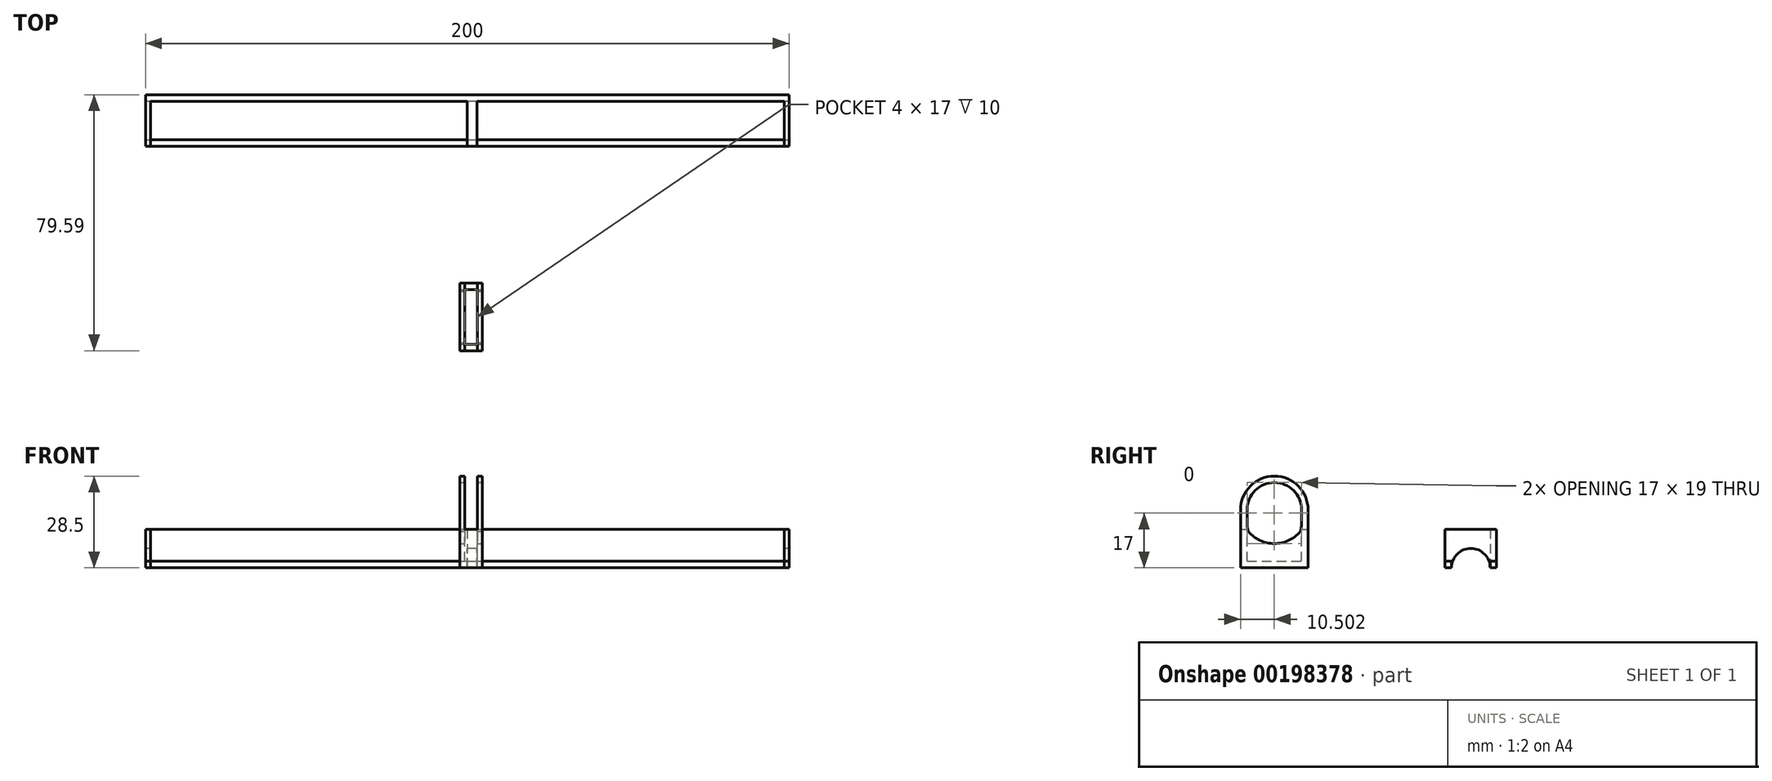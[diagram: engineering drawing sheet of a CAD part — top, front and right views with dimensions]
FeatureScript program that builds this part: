
annotation { "Feature Type Name" : "Feature", "Feature Type Description" : "" }
export const myFeature = defineFeature(function(context is Context, id is Id, definition is map)
    precondition{}
    {
        {
            assignVariable(context, id + "F0", {"name" : "railWidth", "anyValue" : 2});
        }
        {
            assignVariable(context, id + "F1", {"name" : "railSpace", "anyValue" : 12});
        }
        {
            var Q0;
            Q0=qCreatedBy(makeId("Top.planeOp"),FACE);
            var sketch = newSketch(context, id + "F2", { "sketchPlane" : qUnion([Q0])});
            skLineSegment(sketch, "E0", {"start": v(-153.07, 40.7) * mm, "end": v(46.93, 40.7) * mm});
            skLineSegment(sketch, "E1", {"start": v(-153.07, 38.7) * mm, "end": v(46.93, 38.7) * mm});
            skLineSegment(sketch, "E2", {"start": v(-153.07, 40.7) * mm, "end": v(-153.07, 38.7) * mm});
            skLineSegment(sketch, "E3", {"start": v(46.93, 40.7) * mm, "end": v(46.93, 38.7) * mm});
            skLineSegment(sketch, "E4", {"start": v(-153.07, 26.7) * mm, "end": v(46.93, 26.7) * mm});
            skLineSegment(sketch, "E5", {"start": v(-153.07, 24.7) * mm, "end": v(46.93, 24.7) * mm});
            skLineSegment(sketch, "E6", {"start": v(-153.07, 26.7) * mm, "end": v(-153.07, 24.7) * mm});
            skLineSegment(sketch, "E7", {"start": v(46.93, 26.7) * mm, "end": v(46.93, 24.7) * mm});
            skLineSegment(sketch, "E8", {"start": v(-153.07, 40.7) * mm, "end": v(-153.07, 24.7) * mm});
            skLineSegment(sketch, "E9", {"start": v(-151.57, 40.7) * mm, "end": v(-151.57, 24.7) * mm});
            skLineSegment(sketch, "E10", {"start": v(46.93, 40.7) * mm, "end": v(46.93, 24.7) * mm});
            skLineSegment(sketch, "E11", {"start": v(45.43, 40.7) * mm, "end": v(45.43, 24.7) * mm});
            skLineSegment(sketch, "E12", {"start": v(-53.07, 40.7) * mm, "end": v(-53.07, 24.7) * mm});
            skLineSegment(sketch, "E13", {"start": v(-50.07, 40.7) * mm, "end": v(-50.07, 24.7) * mm});
            skSolve(sketch);
        }
        {
            var Q0;
            {var subQ0=sQuery(id+"F2.wireOp",EDGE,"E9");var subQ1=sQuery(id+"F2.wireOp",EDGE,"E0");var subQ2=makeQuery(id+"F2.imprint","INTERSECT",VERTEX,{"derivedFrom":[subQ1,subQ0]});Q0=makeQuery(id+"F2.imprint","IMPRINT",FACE,{"disambiguationData":[TD([[makeQuery(id+"F2.imprint","IMPRINT",EDGE,{"disambiguationData":[TD([[subQ2,-1.0]])],"derivedFrom":subQ1}),-1.0]])]});}
            var Q1;
            {var subQ0=sQuery(id+"F2.wireOp",EDGE,"E12");var subQ1=sQuery(id+"F2.wireOp",EDGE,"E0");var subQ2=makeQuery(id+"F2.imprint","INTERSECT",VERTEX,{"derivedFrom":[subQ1,subQ0]});Q1=makeQuery(id+"F2.imprint","IMPRINT",FACE,{"disambiguationData":[TD([[makeQuery(id+"F2.imprint","IMPRINT",EDGE,{"disambiguationData":[TD([[subQ2,-1.0]])],"derivedFrom":subQ1}),-1.0]])]});}
            var Q2;
            {var subQ0=sQuery(id+"F2.wireOp",EDGE,"E11");var subQ1=sQuery(id+"F2.wireOp",EDGE,"E0");var subQ2=makeQuery(id+"F2.imprint","INTERSECT",VERTEX,{"derivedFrom":[subQ1,subQ0]});Q2=makeQuery(id+"F2.imprint","IMPRINT",FACE,{"disambiguationData":[TD([[makeQuery(id+"F2.imprint","IMPRINT",EDGE,{"disambiguationData":[TD([[subQ2,1.0]])],"derivedFrom":subQ1}),-1.0]])]});}
            var Q3;
            {var subQ0=sQuery(id+"F2.wireOp",EDGE,"E8");var subQ1=sQuery(id+"F2.wireOp",EDGE,"E0");var subQ2=makeQuery(id+"F2.imprint","INTERSECT",VERTEX,{"derivedFrom":[subQ1,subQ0]});Q3=makeQuery(id+"F2.imprint","IMPRINT",FACE,{"disambiguationData":[TD([[makeQuery(id+"F2.imprint","IMPRINT",EDGE,{"disambiguationData":[TD([[subQ2,-1.0]])],"derivedFrom":subQ1}),-1.0]])]});}
            var Q4;
            {var subQ0=sQuery(id+"F2.wireOp",EDGE,"E10");var subQ1=sQuery(id+"F2.wireOp",EDGE,"E0");var subQ2=makeQuery(id+"F2.imprint","INTERSECT",VERTEX,{"derivedFrom":[subQ1,subQ0]});Q4=makeQuery(id+"F2.imprint","IMPRINT",FACE,{"disambiguationData":[TD([[makeQuery(id+"F2.imprint","IMPRINT",EDGE,{"disambiguationData":[TD([[subQ2,1.0]])],"derivedFrom":subQ1}),-1.0]])]});}
            var Q5;
            {var subQ0=sQuery(id+"F2.wireOp",EDGE,"E10");var subQ1=sQuery(id+"F2.wireOp",EDGE,"E4");var subQ2=makeQuery(id+"F2.imprint","INTERSECT",VERTEX,{"derivedFrom":[subQ1,subQ0]});Q5=makeQuery(id+"F2.imprint","IMPRINT",FACE,{"disambiguationData":[TD([[makeQuery(id+"F2.imprint","IMPRINT",EDGE,{"disambiguationData":[TD([[subQ2,1.0]])],"derivedFrom":subQ1}),-1.0]])]});}
            var Q6;
            {var subQ0=sQuery(id+"F2.wireOp",EDGE,"E13");var subQ1=sQuery(id+"F2.wireOp",EDGE,"E4");var subQ2=makeQuery(id+"F2.imprint","INTERSECT",VERTEX,{"derivedFrom":[subQ1,subQ0]});Q6=makeQuery(id+"F2.imprint","IMPRINT",FACE,{"disambiguationData":[TD([[makeQuery(id+"F2.imprint","IMPRINT",EDGE,{"disambiguationData":[TD([[subQ2,-1.0]])],"derivedFrom":subQ1}),-1.0]])]});}
            var Q7;
            {var subQ0=sQuery(id+"F2.wireOp",EDGE,"E12");var subQ1=sQuery(id+"F2.wireOp",EDGE,"E4");var subQ2=makeQuery(id+"F2.imprint","INTERSECT",VERTEX,{"derivedFrom":[subQ1,subQ0]});Q7=makeQuery(id+"F2.imprint","IMPRINT",FACE,{"disambiguationData":[TD([[makeQuery(id+"F2.imprint","IMPRINT",EDGE,{"disambiguationData":[TD([[subQ2,-1.0]])],"derivedFrom":subQ1}),-1.0]])]});}
            var Q8;
            {var subQ0=sQuery(id+"F2.wireOp",EDGE,"E9");var subQ1=sQuery(id+"F2.wireOp",EDGE,"E4");var subQ2=makeQuery(id+"F2.imprint","INTERSECT",VERTEX,{"derivedFrom":[subQ1,subQ0]});Q8=makeQuery(id+"F2.imprint","IMPRINT",FACE,{"disambiguationData":[TD([[makeQuery(id+"F2.imprint","IMPRINT",EDGE,{"disambiguationData":[TD([[subQ2,-1.0]])],"derivedFrom":subQ1}),-1.0]])]});}
            var Q9;
            {var subQ0=sQuery(id+"F2.wireOp",EDGE,"E8");var subQ1=sQuery(id+"F2.wireOp",EDGE,"E4");var subQ2=makeQuery(id+"F2.imprint","INTERSECT",VERTEX,{"derivedFrom":[subQ1,subQ0]});Q9=makeQuery(id+"F2.imprint","IMPRINT",FACE,{"disambiguationData":[TD([[makeQuery(id+"F2.imprint","IMPRINT",EDGE,{"disambiguationData":[TD([[subQ2,-1.0]])],"derivedFrom":subQ1}),-1.0]])]});}
            extrude(context, id + "F3", {"entities" : qUnion([Q0, Q1, Q2, Q3, Q4, Q5, Q6, Q7, Q8, Q9]), "depth" : getVariable(context, 'railWidth') * mm});
        }
        {
            var Q0;
            {var subQ0=sQuery(id+"F2.wireOp",EDGE,"E8");var subQ1=sQuery(id+"F2.wireOp",EDGE,"E1");var subQ2=makeQuery(id+"F2.imprint","INTERSECT",VERTEX,{"derivedFrom":[subQ1,subQ0]});Q0=makeQuery(id+"F2.imprint","IMPRINT",FACE,{"disambiguationData":[TD([[makeQuery(id+"F2.imprint","IMPRINT",EDGE,{"disambiguationData":[TD([[subQ2,-1.0]])],"derivedFrom":subQ1}),-1.0]])]});}
            var Q1;
            {var subQ0=sQuery(id+"F2.wireOp",EDGE,"E12");var subQ1=sQuery(id+"F2.wireOp",EDGE,"E1");var subQ2=makeQuery(id+"F2.imprint","INTERSECT",VERTEX,{"derivedFrom":[subQ1,subQ0]});Q1=makeQuery(id+"F2.imprint","IMPRINT",FACE,{"disambiguationData":[TD([[makeQuery(id+"F2.imprint","IMPRINT",EDGE,{"disambiguationData":[TD([[subQ2,-1.0]])],"derivedFrom":subQ1}),-1.0]])]});}
            var Q2;
            {var subQ0=sQuery(id+"F2.wireOp",EDGE,"E10");var subQ1=sQuery(id+"F2.wireOp",EDGE,"E1");var subQ2=makeQuery(id+"F2.imprint","INTERSECT",VERTEX,{"derivedFrom":[subQ1,subQ0]});Q2=makeQuery(id+"F2.imprint","IMPRINT",FACE,{"disambiguationData":[TD([[makeQuery(id+"F2.imprint","IMPRINT",EDGE,{"disambiguationData":[TD([[subQ2,1.0]])],"derivedFrom":subQ1}),-1.0]])]});}
            var Q3;
            {var subQ0=sQuery(id+"F2.wireOp",EDGE,"E8");var subQ1=sQuery(id+"F2.wireOp",EDGE,"E4");var subQ2=makeQuery(id+"F2.imprint","INTERSECT",VERTEX,{"derivedFrom":[subQ1,subQ0]});Q3=makeQuery(id+"F2.imprint","IMPRINT",FACE,{"disambiguationData":[TD([[makeQuery(id+"F2.imprint","IMPRINT",EDGE,{"disambiguationData":[TD([[subQ2,-1.0]])],"derivedFrom":subQ1}),-1.0]])]});}
            var Q4;
            {var subQ0=sQuery(id+"F2.wireOp",EDGE,"E8");var subQ1=sQuery(id+"F2.wireOp",EDGE,"E0");var subQ2=makeQuery(id+"F2.imprint","INTERSECT",VERTEX,{"derivedFrom":[subQ1,subQ0]});Q4=makeQuery(id+"F2.imprint","IMPRINT",FACE,{"disambiguationData":[TD([[makeQuery(id+"F2.imprint","IMPRINT",EDGE,{"disambiguationData":[TD([[subQ2,-1.0]])],"derivedFrom":subQ1}),-1.0]])]});}
            var Q5;
            {var subQ0=sQuery(id+"F2.wireOp",EDGE,"E12");var subQ1=sQuery(id+"F2.wireOp",EDGE,"E4");var subQ2=makeQuery(id+"F2.imprint","INTERSECT",VERTEX,{"derivedFrom":[subQ1,subQ0]});Q5=makeQuery(id+"F2.imprint","IMPRINT",FACE,{"disambiguationData":[TD([[makeQuery(id+"F2.imprint","IMPRINT",EDGE,{"disambiguationData":[TD([[subQ2,-1.0]])],"derivedFrom":subQ1}),-1.0]])]});}
            var Q6;
            {var subQ0=sQuery(id+"F2.wireOp",EDGE,"E12");var subQ1=sQuery(id+"F2.wireOp",EDGE,"E0");var subQ2=makeQuery(id+"F2.imprint","INTERSECT",VERTEX,{"derivedFrom":[subQ1,subQ0]});Q6=makeQuery(id+"F2.imprint","IMPRINT",FACE,{"disambiguationData":[TD([[makeQuery(id+"F2.imprint","IMPRINT",EDGE,{"disambiguationData":[TD([[subQ2,-1.0]])],"derivedFrom":subQ1}),-1.0]])]});}
            var Q7;
            {var subQ0=sQuery(id+"F2.wireOp",EDGE,"E10");var subQ1=sQuery(id+"F2.wireOp",EDGE,"E4");var subQ2=makeQuery(id+"F2.imprint","INTERSECT",VERTEX,{"derivedFrom":[subQ1,subQ0]});Q7=makeQuery(id+"F2.imprint","IMPRINT",FACE,{"disambiguationData":[TD([[makeQuery(id+"F2.imprint","IMPRINT",EDGE,{"disambiguationData":[TD([[subQ2,1.0]])],"derivedFrom":subQ1}),-1.0]])]});}
            var Q8;
            {var subQ0=sQuery(id+"F2.wireOp",EDGE,"E10");var subQ1=sQuery(id+"F2.wireOp",EDGE,"E0");var subQ2=makeQuery(id+"F2.imprint","INTERSECT",VERTEX,{"derivedFrom":[subQ1,subQ0]});Q8=makeQuery(id+"F2.imprint","IMPRINT",FACE,{"disambiguationData":[TD([[makeQuery(id+"F2.imprint","IMPRINT",EDGE,{"disambiguationData":[TD([[subQ2,1.0]])],"derivedFrom":subQ1}),-1.0]])]});}
            extrude(context, id + "F4", {"entities" : qUnion([Q0, Q1, Q2, Q3, Q4, Q5, Q6, Q7, Q8]), "depth" : (getVariable(context, 'railSpace')) * mm});
        }
        {
            var Q0;
            Q0=makeQuery(id+"F4.opExtrude","SWEPT_FACE",FACE,{"disambiguationData":[OSD([sQuery(id+"F2.wireOp",EDGE,"E8")])]});
            var sketch = newSketch(context, id + "F5", { "sketchPlane" : qUnion([Q0])});
            skPoint(sketch, "E14", {"position": v(-32.7, 0) * mm});
            skCircle(sketch, "E15", {"center": v(-32.7, 0) * mm, "radius": 6 * mm});
            skSolve(sketch);
        }
        {
            var Q0;
            {var subQ0=sQuery(id+"F5.wireOp",EDGE,"E15");var subQ1=makeQuery(id+"F4.opExtrude","CAP_EDGE",EDGE,{"disambiguationData":[OSD([sQuery(id+"F2.wireOp",EDGE,"E8")])],"isStart":true});var subQ2=makeQuery(id+"F5.imprint","INTERSECT",VERTEX,{"disambiguationData":[OD(0.0)],"derivedFrom":[subQ1,subQ0]});Q0=makeQuery(id+"F5.imprint","IMPRINT",FACE,{"disambiguationData":[TD([[makeQuery(id+"F5.imprint","IMPRINT",EDGE,{"disambiguationData":[TD([[subQ2,1.0]])],"derivedFrom":subQ0}),1.0]])]});}
            extrude(context, id + "F6", {"entities" : qUnion([Q0]), "operationType" : NewBodyOperationType.REMOVE, "endBound" : BoundingType.THROUGH_ALL, "oppositeDirection" : true, "depth" : 25 * mm});
        }
        {
            var Q0;
            Q0=qCreatedBy(makeId("Top.planeOp"),FACE);
            var sketch = newSketch(context, id + "F7", { "sketchPlane" : qUnion([Q0])});
            skLineSegment(sketch, "E16.bottom", {"start": v(-55.4, -17.9) * mm, "end": v(-48.4, -17.9) * mm});
            skLineSegment(sketch, "E16.top", {"start": v(-55.4, -38.9) * mm, "end": v(-48.4, -38.9) * mm});
            skLineSegment(sketch, "E16.left", {"start": v(-55.4, -17.9) * mm, "end": v(-55.4, -38.9) * mm});
            skLineSegment(sketch, "E16.right", {"start": v(-48.4, -17.9) * mm, "end": v(-48.4, -38.9) * mm});
            skSolve(sketch);
        }
        {
            var Q0;
            Q0=makeQuery(id+"F7.imprint","IMPRINT",FACE,{"disambiguationData":[TD([[makeQuery(id+"F7.imprint","IMPRINT",EDGE,{"derivedFrom":sQuery(id+"F7.wireOp",EDGE,"E16.bottom")}),-1.0]])]});
            extrude(context, id + "F8", {"entities" : qUnion([Q0]), "depth" : 3 * getVariable(context, 'railSpace') * mm});
        }
        {
            var Q0;
            Q0=makeQuery(id+"F8.opExtrude","CAP_FACE",FACE,{"disambiguationData":[OSD([sQuery(id+"F7.wireOp",EDGE,"E16.bottom"),sQuery(id+"F7.wireOp",EDGE,"E16.top"),sQuery(id+"F7.wireOp",EDGE,"E16.left"),sQuery(id+"F7.wireOp",EDGE,"E16.right")])],"isStart":false});
            var sketch = newSketch(context, id + "F9", { "sketchPlane" : qUnion([Q0])});
            skLineSegment(sketch, "E17", {"start": v(-55.4, -36.9) * mm, "end": v(-48.4, -36.9) * mm});
            skLineSegment(sketch, "E18", {"start": v(-55.4, -19.9) * mm, "end": v(-48.4, -19.9) * mm});
            skLineSegment(sketch, "E19", {"start": v(-53.9, -38.9) * mm, "end": v(-53.9, -17.9) * mm});
            skLineSegment(sketch, "E20", {"start": v(-49.9, -38.9) * mm, "end": v(-49.9, -17.9) * mm});
            skSolve(sketch);
        }
        {
            var Q0;
            {var subQ0=sQuery(id+"F9.wireOp",EDGE,"E19");var subQ1=sQuery(id+"F9.wireOp",EDGE,"E17");var subQ2=makeQuery(id+"F9.imprint","INTERSECT",VERTEX,{"derivedFrom":[subQ1,subQ0]});Q0=makeQuery(id+"F9.imprint","IMPRINT",FACE,{"disambiguationData":[TD([[makeQuery(id+"F9.imprint","IMPRINT",EDGE,{"disambiguationData":[TD([[subQ2,-1.0]])],"derivedFrom":subQ1}),1.0]])]});}
            extrude(context, id + "F10", {"entities" : qUnion([Q0]), "operationType" : NewBodyOperationType.REMOVE, "oppositeDirection" : true, "depth" : (3 * getVariable(context, 'railSpace') - getVariable(context, 'railWidth')) * mm});
        }
        {
            var Q0;
            {var subQ0=sQuery(id+"F9.wireOp",EDGE,"E19");var subQ1=sQuery(id+"F9.wireOp",EDGE,"E17");var subQ2=makeQuery(id+"F9.imprint","INTERSECT",VERTEX,{"derivedFrom":[subQ1,subQ0]});Q0=makeQuery(id+"F9.imprint","IMPRINT",FACE,{"disambiguationData":[TD([[makeQuery(id+"F9.imprint","IMPRINT",EDGE,{"disambiguationData":[TD([[subQ2,-1.0]])],"derivedFrom":subQ1}),-1.0]])]});}
            var Q1;
            {var subQ0=sQuery(id+"F9.wireOp",EDGE,"E19");var subQ1=sQuery(id+"F9.wireOp",EDGE,"E18");var subQ2=makeQuery(id+"F9.imprint","INTERSECT",VERTEX,{"derivedFrom":[subQ1,subQ0]});Q1=makeQuery(id+"F9.imprint","IMPRINT",FACE,{"disambiguationData":[TD([[makeQuery(id+"F9.imprint","IMPRINT",EDGE,{"disambiguationData":[TD([[subQ2,-1.0]])],"derivedFrom":subQ1}),1.0]])]});}
            extrude(context, id + "F11", {"entities" : qUnion([Q0, Q1]), "operationType" : NewBodyOperationType.REMOVE, "oppositeDirection" : true, "depth" : (2 * getVariable(context, 'railSpace')) * mm});
        }
        {
            var Q0;
            Q0=makeQuery(id+"F8.opExtrude","SWEPT_FACE",FACE,{"disambiguationData":[OSD([sQuery(id+"F7.wireOp",EDGE,"E16.right")])]});
            var sketch = newSketch(context, id + "F12", { "sketchPlane" : qUnion([Q0])});
            skPoint(sketch, "E21", {"position": v(-28.4, 36) * mm});
            skPoint(sketch, "E22", {"position": v(-38.9, 24) * mm});
            skPoint(sketch, "E23", {"position": v(-17.9, 24) * mm});
            skPoint(sketch, "E24", {"position": v(-36.9, 36) * mm});
            skPoint(sketch, "E25", {"position": v(-19.9, 36) * mm});
            skLineSegment(sketch, "E26", {"start": v(-36.9, 36) * mm, "end": v(-36.9, 0) * mm});
            skLineSegment(sketch, "E27", {"start": v(-19.9, 36) * mm, "end": v(-19.9, 0) * mm});
            skLineSegment(sketch, "E28", {"start": v(-38.9, 14) * mm, "end": v(-17.9, 14) * mm});
            skPoint(sketch, "E29", {"position": v(-28.4, 14) * mm});
            skCircle(sketch, "E30", {"center": v(-28.4, 14) * mm, "radius": 8.5 * mm});
            skLineSegment(sketch, "E31", {"start": v(-17.9, 18) * mm, "end": v(-38.9, 18) * mm});
            skPoint(sketch, "E32", {"position": v(-28.4, 18) * mm});
            skCircle(sketch, "E33", {"center": v(-28.4, 18) * mm, "radius": 8.5 * mm});
            skCircle(sketch, "E34", {"center": v(-28.4, 18) * mm, "radius": 10.5 * mm});
            skSolve(sketch);
        }
        {
            var Q0;
            {var subQ0=sQuery(id+"F12.wireOp",EDGE,"E34");var subQ1=sQuery(id+"F12.wireOp",EDGE,"E30");var subQ2=makeQuery(id+"F12.imprint","INTERSECT",VERTEX,{"disambiguationData":[OD(0.0)],"derivedFrom":[subQ1,subQ0]});Q0=makeQuery(id+"F12.imprint","IMPRINT",FACE,{"disambiguationData":[TD([[makeQuery(id+"F12.imprint","IMPRINT",EDGE,{"disambiguationData":[TD([[subQ2,-1.0]])],"derivedFrom":subQ1}),1.0]])]});}
            var Q1;
            {var subQ3=sQuery(id+"F12.wireOp",EDGE,"E28");var subQ5=sQuery(id+"F12.wireOp",EDGE,"E33");var subQ9=makeQuery(id+"F12.imprint","INTERSECT",VERTEX,{"disambiguationData":[OD(0.0)],"derivedFrom":[subQ3,subQ5]});Q1=makeQuery(id+"F12.imprint","IMPRINT",FACE,{"disambiguationData":[TD([[makeQuery(id+"F12.imprint","IMPRINT",EDGE,{"disambiguationData":[TD([[subQ9,-1.0]])],"derivedFrom":subQ5}),-1.0]])]});}
            var Q2;
            {var subQ0=sQuery(id+"F12.wireOp",EDGE,"E33");var subQ1=sQuery(id+"F12.wireOp",EDGE,"E28");var subQ2=makeQuery(id+"F12.imprint","INTERSECT",VERTEX,{"disambiguationData":[OD(0.0)],"derivedFrom":[subQ1,subQ0]});Q2=makeQuery(id+"F12.imprint","IMPRINT",FACE,{"disambiguationData":[TD([[makeQuery(id+"F12.imprint","IMPRINT",EDGE,{"disambiguationData":[TD([[subQ2,-1.0]])],"derivedFrom":subQ1}),-1.0]])]});}
            var Q3;
            {var subQ4=sQuery(id+"F12.wireOp",EDGE,"E33");var subQ7=sQuery(id+"F12.wireOp",EDGE,"E28");var subQ8=makeQuery(id+"F12.imprint","INTERSECT",VERTEX,{"disambiguationData":[OD(0.0)],"derivedFrom":[subQ7,subQ4]});Q3=makeQuery(id+"F12.imprint","IMPRINT",FACE,{"disambiguationData":[TD([[makeQuery(id+"F12.imprint","IMPRINT",EDGE,{"disambiguationData":[TD([[subQ8,-1.0]])],"derivedFrom":subQ7}),1.0]])]});}
            var Q4;
            {var subQ0=sQuery(id+"F12.wireOp",EDGE,"E31");var subQ1=sQuery(id+"F12.wireOp",EDGE,"E30");var subQ2=makeQuery(id+"F12.imprint","INTERSECT",VERTEX,{"disambiguationData":[OD(1.0)],"derivedFrom":[subQ1,subQ0]});Q4=makeQuery(id+"F12.imprint","IMPRINT",FACE,{"disambiguationData":[TD([[makeQuery(id+"F12.imprint","IMPRINT",EDGE,{"disambiguationData":[TD([[subQ2,-1.0]])],"derivedFrom":subQ1}),-1.0]])]});}
            var Q5;
            {var subQ0=sQuery(id+"F12.wireOp",EDGE,"E31");var subQ1=sQuery(id+"F12.wireOp",EDGE,"E30");var subQ2=makeQuery(id+"F12.imprint","INTERSECT",VERTEX,{"disambiguationData":[OD(0.0)],"derivedFrom":[subQ1,subQ0]});Q5=makeQuery(id+"F12.imprint","IMPRINT",FACE,{"disambiguationData":[TD([[makeQuery(id+"F12.imprint","IMPRINT",EDGE,{"disambiguationData":[TD([[subQ2,-1.0]])],"derivedFrom":subQ1}),1.0]])]});}
            var Q6;
            {var subQ0=sQuery(id+"F12.wireOp",EDGE,"E33");var subQ1=sQuery(id+"F12.wireOp",EDGE,"E28");var subQ2=makeQuery(id+"F12.imprint","INTERSECT",VERTEX,{"disambiguationData":[OD(1.0)],"derivedFrom":[subQ1,subQ0]});Q6=makeQuery(id+"F12.imprint","IMPRINT",FACE,{"disambiguationData":[TD([[makeQuery(id+"F12.imprint","IMPRINT",EDGE,{"disambiguationData":[TD([[subQ2,-1.0]])],"derivedFrom":subQ0}),-1.0]])]});}
            var Q7;
            {var subQ0=sQuery(id+"F12.wireOp",EDGE,"E33");var subQ3=sQuery(id+"F12.wireOp",EDGE,"E30");var subQ5=makeQuery(id+"F12.imprint","INTERSECT",VERTEX,{"disambiguationData":[OD(0.0)],"derivedFrom":[subQ3,subQ0]});Q7=makeQuery(id+"F12.imprint","IMPRINT",FACE,{"disambiguationData":[TD([[makeQuery(id+"F12.imprint","IMPRINT",EDGE,{"disambiguationData":[TD([[subQ5,1.0]])],"derivedFrom":subQ3}),-1.0]])]});}
            var Q8;
            {var subQ0=sQuery(id+"F12.wireOp",EDGE,"E33");var subQ1=sQuery(id+"F12.wireOp",EDGE,"E30");var subQ2=makeQuery(id+"F12.imprint","INTERSECT",VERTEX,{"disambiguationData":[OD(0.0)],"derivedFrom":[subQ1,subQ0]});Q8=makeQuery(id+"F12.imprint","IMPRINT",FACE,{"disambiguationData":[TD([[makeQuery(id+"F12.imprint","IMPRINT",EDGE,{"disambiguationData":[TD([[subQ2,-1.0]])],"derivedFrom":subQ1}),-1.0]])]});}
            var Q9;
            {var subQ0=sQuery(id+"F12.wireOp",EDGE,"E31");var subQ1=sQuery(id+"F12.wireOp",EDGE,"E30");var subQ2=makeQuery(id+"F12.imprint","INTERSECT",VERTEX,{"disambiguationData":[OD(0.0)],"derivedFrom":[subQ1,subQ0]});Q9=makeQuery(id+"F12.imprint","IMPRINT",FACE,{"disambiguationData":[TD([[makeQuery(id+"F12.imprint","IMPRINT",EDGE,{"disambiguationData":[TD([[subQ2,-1.0]])],"derivedFrom":subQ1}),-1.0]])]});}
            var Q10;
            {var subQ0=sQuery(id+"F12.wireOp",EDGE,"E33");var subQ3=sQuery(id+"F12.wireOp",EDGE,"E30");var subQ5=makeQuery(id+"F12.imprint","INTERSECT",VERTEX,{"disambiguationData":[OD(1.0)],"derivedFrom":[subQ3,subQ0]});Q10=makeQuery(id+"F12.imprint","IMPRINT",FACE,{"disambiguationData":[TD([[makeQuery(id+"F12.imprint","IMPRINT",EDGE,{"disambiguationData":[TD([[subQ5,-1.0]])],"derivedFrom":subQ3}),-1.0]])]});}
            var Q11;
            {var subQ0=sQuery(id+"F12.wireOp",EDGE,"E33");var subQ1=sQuery(id+"F12.wireOp",EDGE,"E28");var subQ2=makeQuery(id+"F12.imprint","INTERSECT",VERTEX,{"disambiguationData":[OD(0.0)],"derivedFrom":[subQ1,subQ0]});Q11=makeQuery(id+"F12.imprint","IMPRINT",FACE,{"disambiguationData":[TD([[makeQuery(id+"F12.imprint","IMPRINT",EDGE,{"disambiguationData":[TD([[subQ2,1.0]])],"derivedFrom":subQ0}),-1.0]])]});}
            var Q12;
            {var subQ0=sQuery(id+"F12.wireOp",EDGE,"E26");var subQ1=sQuery(id+"F7.wireOp",EDGE,"E16.right");var subQ2=makeQuery(id+"F8.opExtrude","CAP_EDGE",EDGE,{"disambiguationData":[OSD([subQ1])],"isStart":false});var subQ3=makeQuery(id+"F12.imprint","INTERSECT",VERTEX,{"derivedFrom":[subQ2,subQ0]});Q12=makeQuery(id+"F12.imprint","IMPRINT",FACE,{"disambiguationData":[TD([[makeQuery(id+"F12.imprint","IMPRINT",EDGE,{"disambiguationData":[TD([[subQ3,-1.0]])],"derivedFrom":subQ0}),-1.0]])]});}
            var Q13;
            {var subQ0=sQuery(id+"F12.wireOp",EDGE,"E26");var subQ1=makeQuery(id+"F8.opExtrude","CAP_EDGE",EDGE,{"disambiguationData":[OSD([sQuery(id+"F7.wireOp",EDGE,"E16.right")])],"isStart":false});var subQ2=makeQuery(id+"F12.imprint","INTERSECT",VERTEX,{"derivedFrom":[subQ1,subQ0]});Q13=makeQuery(id+"F12.imprint","IMPRINT",FACE,{"disambiguationData":[TD([[makeQuery(id+"F12.imprint","IMPRINT",EDGE,{"disambiguationData":[TD([[subQ2,-1.0]])],"derivedFrom":subQ0}),1.0]])]});}
            var Q14;
            {var subQ0=sQuery(id+"F12.wireOp",EDGE,"E27");var subQ1=sQuery(id+"F7.wireOp",EDGE,"E16.right");var subQ2=makeQuery(id+"F8.opExtrude","CAP_EDGE",EDGE,{"disambiguationData":[OSD([subQ1])],"isStart":false});var subQ3=makeQuery(id+"F12.imprint","INTERSECT",VERTEX,{"derivedFrom":[subQ2,subQ0]});Q14=makeQuery(id+"F12.imprint","IMPRINT",FACE,{"disambiguationData":[TD([[makeQuery(id+"F12.imprint","IMPRINT",EDGE,{"disambiguationData":[TD([[subQ3,-1.0]])],"derivedFrom":subQ0}),1.0]])]});}
            extrude(context, id + "F13", {"entities" : qUnion([Q0, Q1, Q2, Q3, Q4, Q5, Q6, Q7, Q8, Q9, Q10, Q11, Q12, Q13, Q14]), "operationType" : NewBodyOperationType.REMOVE, "endBound" : BoundingType.THROUGH_ALL, "oppositeDirection" : true, "depth" : 25 * mm});
        }
    });
